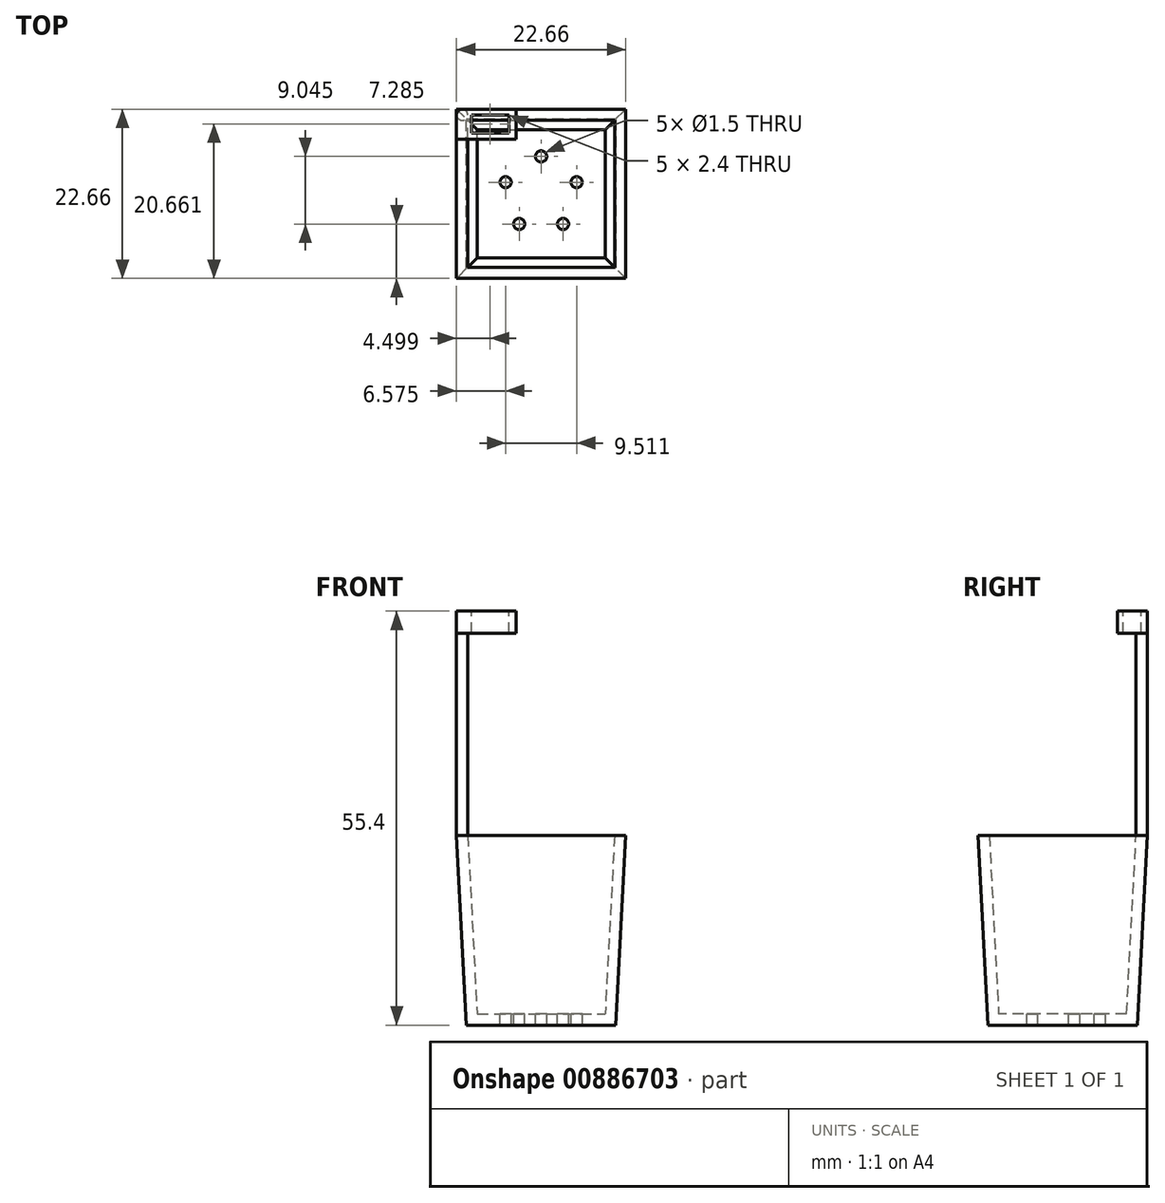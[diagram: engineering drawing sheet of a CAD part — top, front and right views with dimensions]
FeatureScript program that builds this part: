
annotation { "Feature Type Name" : "Feature", "Feature Type Description" : "" }
export const myFeature = defineFeature(function(context is Context, id is Id, definition is map)
    precondition{}
    {
        {
            var Q0;
            Q0=qCreatedBy(makeId("Top.planeOp"),FACE);
            var sketch = newSketch(context, id + "F0", { "sketchPlane" : qUnion([Q0])});
            skLineSegment(sketch, "E0.bottom", {"start": v(10, 10) * mm, "end": v(-10, 10) * mm});
            skLineSegment(sketch, "E0.top", {"start": v(10, -10) * mm, "end": v(-10, -10) * mm});
            skLineSegment(sketch, "E0.left", {"start": v(10, 10) * mm, "end": v(10, -10) * mm});
            skLineSegment(sketch, "E0.right", {"start": v(-10, 10) * mm, "end": v(-10, -10) * mm});
            skPoint(sketch, "E0.middle", {"position": v(0, 0) * mm});
            skSolve(sketch);
        }
        {
            var Q0;
            Q0 = qSketchRegion(id + "F0", true);
            extrude(context, id + "F1", {"entities" : qUnion([Q0]), "depth" : 25.4 * mm, "offsetDistance" : 25.4 * mm, "hasDraft" : true, "draftAngle" : 3 * degree});
        }
        {
            var Q0;
            Q0=makeQuery(id+"F1.opExtrude","CAP_FACE",FACE,{"disambiguationData":[OSD([sQuery(id+"F0.wireOp",EDGE,"E0.bottom"),sQuery(id+"F0.wireOp",EDGE,"E0.top"),sQuery(id+"F0.wireOp",EDGE,"E0.left"),sQuery(id+"F0.wireOp",EDGE,"E0.right")])],"isStart":false});
            shell(context, id + "F2", {"entities" : qUnion([Q0]), "thickness" : 1.5 * mm});
        }
        {
            var Q0;
            Q0=makeQuery(id+"F2.opShell","OFFSET_FACE",FACE,{"disambiguationData":[OSD([sQuery(id+"F0.wireOp",EDGE,"E0.bottom"),sQuery(id+"F0.wireOp",EDGE,"E0.top"),sQuery(id+"F0.wireOp",EDGE,"E0.left"),sQuery(id+"F0.wireOp",EDGE,"E0.right")])]});
            var sketch = newSketch(context, id + "F3", { "sketchPlane" : qUnion([Q0])});
            skCircle(sketch, "E1", {"center": v(0, 5) * mm, "radius": 0.75 * mm});
            skCircle(sketch, "E2.1.0", {"center": v(-4.76, 1.55) * mm, "radius": 0.75 * mm});
            skCircle(sketch, "E2.2.0", {"center": v(-2.94, -4.05) * mm, "radius": 0.75 * mm});
            skCircle(sketch, "E2.3.0", {"center": v(2.94, -4.05) * mm, "radius": 0.75 * mm});
            skCircle(sketch, "E2.4.0", {"center": v(4.76, 1.55) * mm, "radius": 0.75 * mm});
            skPoint(sketch, "E2.center", {"position": v(0, 0) * mm});
            skSolve(sketch);
        }
        {
            var Q0;
            Q0=makeQuery(id+"F3.imprint","IMPRINT",FACE,{"disambiguationData":[TD([[makeQuery(id+"F3.imprint","IMPRINT",EDGE,{"derivedFrom":sQuery(id+"F3.wireOp",EDGE,"E1")}),1.0]])]});
            var Q1;
            Q1=makeQuery(id+"F3.imprint","IMPRINT",FACE,{"disambiguationData":[TD([[makeQuery(id+"F3.imprint","IMPRINT",EDGE,{"derivedFrom":sQuery(id+"F3.wireOp",EDGE,"E2.4.0")}),1.0]])]});
            var Q2;
            Q2=makeQuery(id+"F3.imprint","IMPRINT",FACE,{"disambiguationData":[TD([[makeQuery(id+"F3.imprint","IMPRINT",EDGE,{"derivedFrom":sQuery(id+"F3.wireOp",EDGE,"E2.3.0")}),1.0]])]});
            var Q3;
            Q3=makeQuery(id+"F3.imprint","IMPRINT",FACE,{"disambiguationData":[TD([[makeQuery(id+"F3.imprint","IMPRINT",EDGE,{"derivedFrom":sQuery(id+"F3.wireOp",EDGE,"E2.2.0")}),1.0]])]});
            var Q4;
            Q4=makeQuery(id+"F3.imprint","IMPRINT",FACE,{"disambiguationData":[TD([[makeQuery(id+"F3.imprint","IMPRINT",EDGE,{"derivedFrom":sQuery(id+"F3.wireOp",EDGE,"E2.1.0")}),1.0]])]});
            extrude(context, id + "F4", {"entities" : qUnion([Q0, Q1, Q2, Q3, Q4]), "operationType" : NewBodyOperationType.REMOVE, "endBound" : BoundingType.THROUGH_ALL, "oppositeDirection" : true, "depth" : 25.4 * mm, "offsetDistance" : 25.4 * mm});
        }
        {
            var Q0;
            Q0=makeQuery(id+"F1.opExtrude","CAP_FACE",FACE,{"disambiguationData":[OSD([sQuery(id+"F0.wireOp",EDGE,"E0.bottom"),sQuery(id+"F0.wireOp",EDGE,"E0.top"),sQuery(id+"F0.wireOp",EDGE,"E0.left"),sQuery(id+"F0.wireOp",EDGE,"E0.right")])],"isStart":false});
            var sketch = newSketch(context, id + "F5", { "sketchPlane" : qUnion([Q0])});
            skCircle(sketch, "E3", {"center": v(-10.58, 10.58) * mm, "radius": 0.75 * mm});
            skSolve(sketch);
        }
        {
            var Q0;
            {var subQ0=sQuery(id+"F5.wireOp",EDGE,"E3");var subQ1=makeQuery(id+"F5.imprint","INTERSECT",VERTEX,{"derivedFrom":[makeQuery(id+"F1.opExtrude","CAP_EDGE",EDGE,{"disambiguationData":[OSD([sQuery(id+"F0.wireOp",EDGE,"E0.bottom")])],"isStart":false}),subQ0]});Q0=makeQuery(id+"F5.imprint","IMPRINT",FACE,{"disambiguationData":[TD([[makeQuery(id+"F5.imprint","IMPRINT",EDGE,{"disambiguationData":[TD([[subQ1,-1.0]])],"derivedFrom":subQ0}),1.0]])]});}
            extrude(context, id + "F6", {"entities" : qUnion([Q0]), "operationType" : NewBodyOperationType.ADD, "depth" : 30 * mm, "offsetDistance" : 25.4 * mm});
        }
        {
            var Q0;
            Q0=makeQuery(id+"F6.opExtrude","CAP_FACE",FACE,{"disambiguationData":[OSD([sQuery(id+"F5.wireOp",EDGE,"E3")])],"isStart":false});
            var sketch = newSketch(context, id + "F7", { "sketchPlane" : qUnion([Q0])});
            skLineSegment(sketch, "E4.bottom", {"start": v(-11.33, 11.33) * mm, "end": v(-3.33, 11.33) * mm});
            skLineSegment(sketch, "E4.top", {"start": v(-11.33, 7.33) * mm, "end": v(-3.33, 7.33) * mm});
            skLineSegment(sketch, "E4.left", {"start": v(-11.33, 11.33) * mm, "end": v(-11.33, 7.33) * mm});
            skLineSegment(sketch, "E4.right", {"start": v(-3.33, 11.33) * mm, "end": v(-3.33, 7.33) * mm});
            skLineSegment(sketch, "E5.bottom", {"start": v(-9.33, 10.53) * mm, "end": v(-4.33, 10.53) * mm});
            skLineSegment(sketch, "E5.top", {"start": v(-9.33, 8.13) * mm, "end": v(-4.33, 8.13) * mm});
            skLineSegment(sketch, "E5.left", {"start": v(-9.33, 10.53) * mm, "end": v(-9.33, 8.13) * mm});
            skLineSegment(sketch, "E5.right", {"start": v(-4.33, 10.53) * mm, "end": v(-4.33, 8.13) * mm});
            skSolve(sketch);
        }
        {
            var Q0;
            {var subQ2=sQuery(id+"F7.wireOp",EDGE,"E4.top");Q0=makeQuery(id+"F7.imprint","IMPRINT",FACE,{"disambiguationData":[TD([[makeQuery(id+"F7.imprint","IMPRINT",EDGE,{"derivedFrom":subQ2}),1.0]])]});}
            extrude(context, id + "F8", {"entities" : qUnion([Q0]), "operationType" : NewBodyOperationType.ADD, "oppositeDirection" : true, "depth" : 3 * mm, "offsetDistance" : 25.4 * mm});
        }
    });
